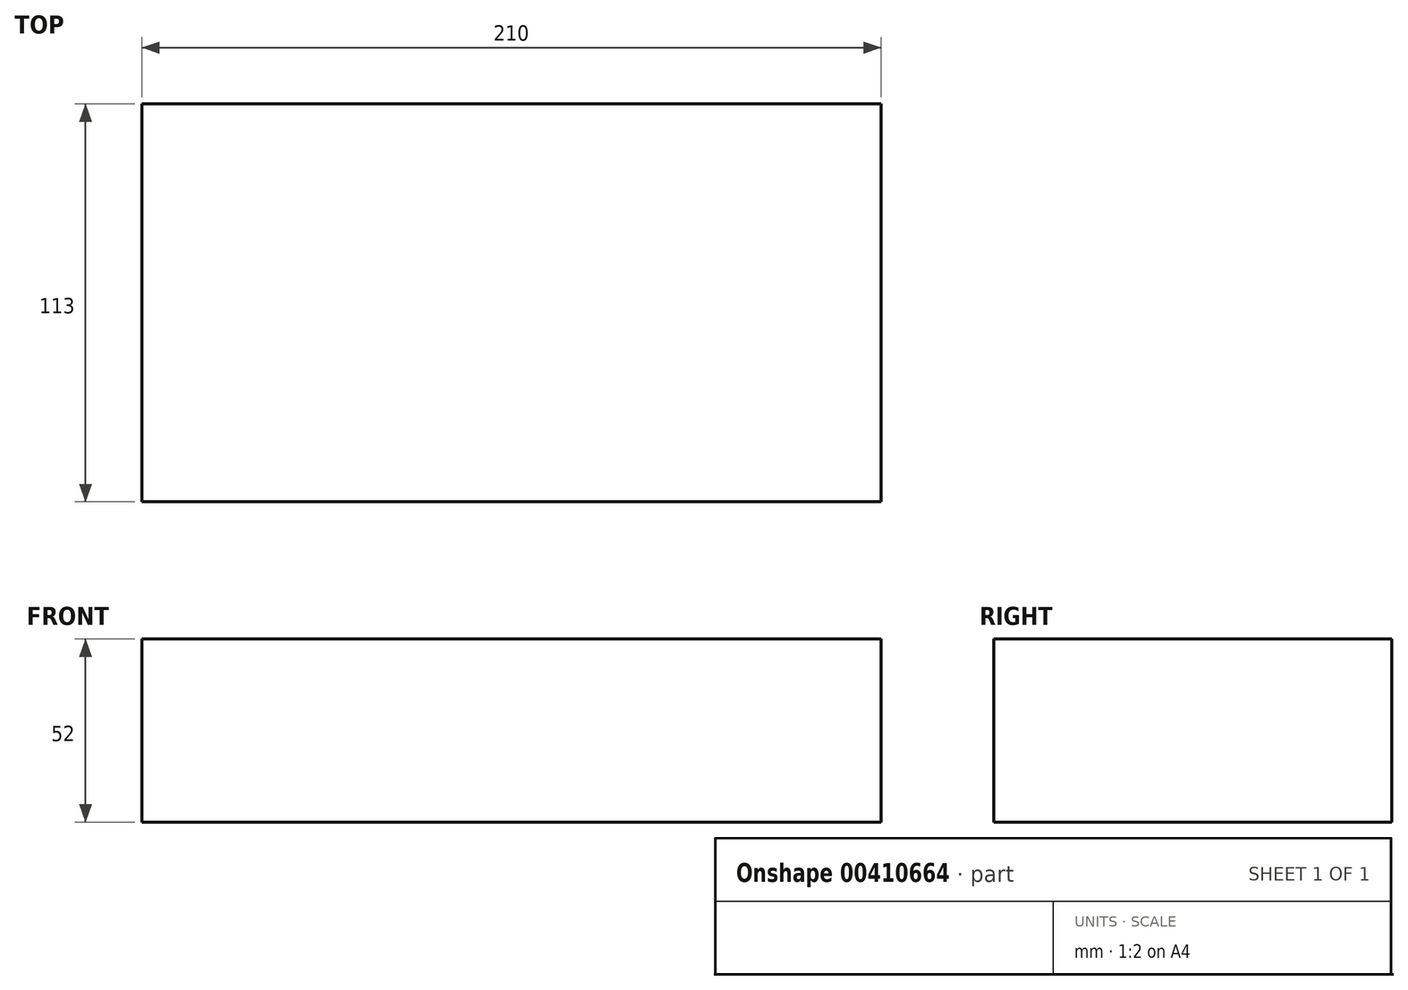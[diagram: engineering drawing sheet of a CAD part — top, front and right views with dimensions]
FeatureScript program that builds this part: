
annotation { "Feature Type Name" : "Feature", "Feature Type Description" : "" }
export const myFeature = defineFeature(function(context is Context, id is Id, definition is map)
    precondition{}
    {
        {
            var Q0;
            Q0=qCreatedBy(makeId("Front.planeOp"),FACE);
            var sketch = newSketch(context, id + "F0", { "sketchPlane" : qUnion([Q0])});
            skLineSegment(sketch, "E0.bottom", {"start": v(105, 26) * mm, "end": v(-105, 26) * mm});
            skLineSegment(sketch, "E0.top", {"start": v(105, -26) * mm, "end": v(-105, -26) * mm});
            skLineSegment(sketch, "E0.left", {"start": v(105, 26) * mm, "end": v(105, -26) * mm});
            skLineSegment(sketch, "E0.right", {"start": v(-105, 26) * mm, "end": v(-105, -26) * mm});
            skPoint(sketch, "E0.middle", {"position": v(0, 0) * mm});
            skSolve(sketch);
        }
        {
            var Q0;
            Q0 = qSketchRegion(id + "F0", true);
            extrude(context, id + "F1", {"entities" : qUnion([Q0]), "endBound" : BoundingType.SYMMETRIC, "depth" : 113 * mm});
        }
    });
